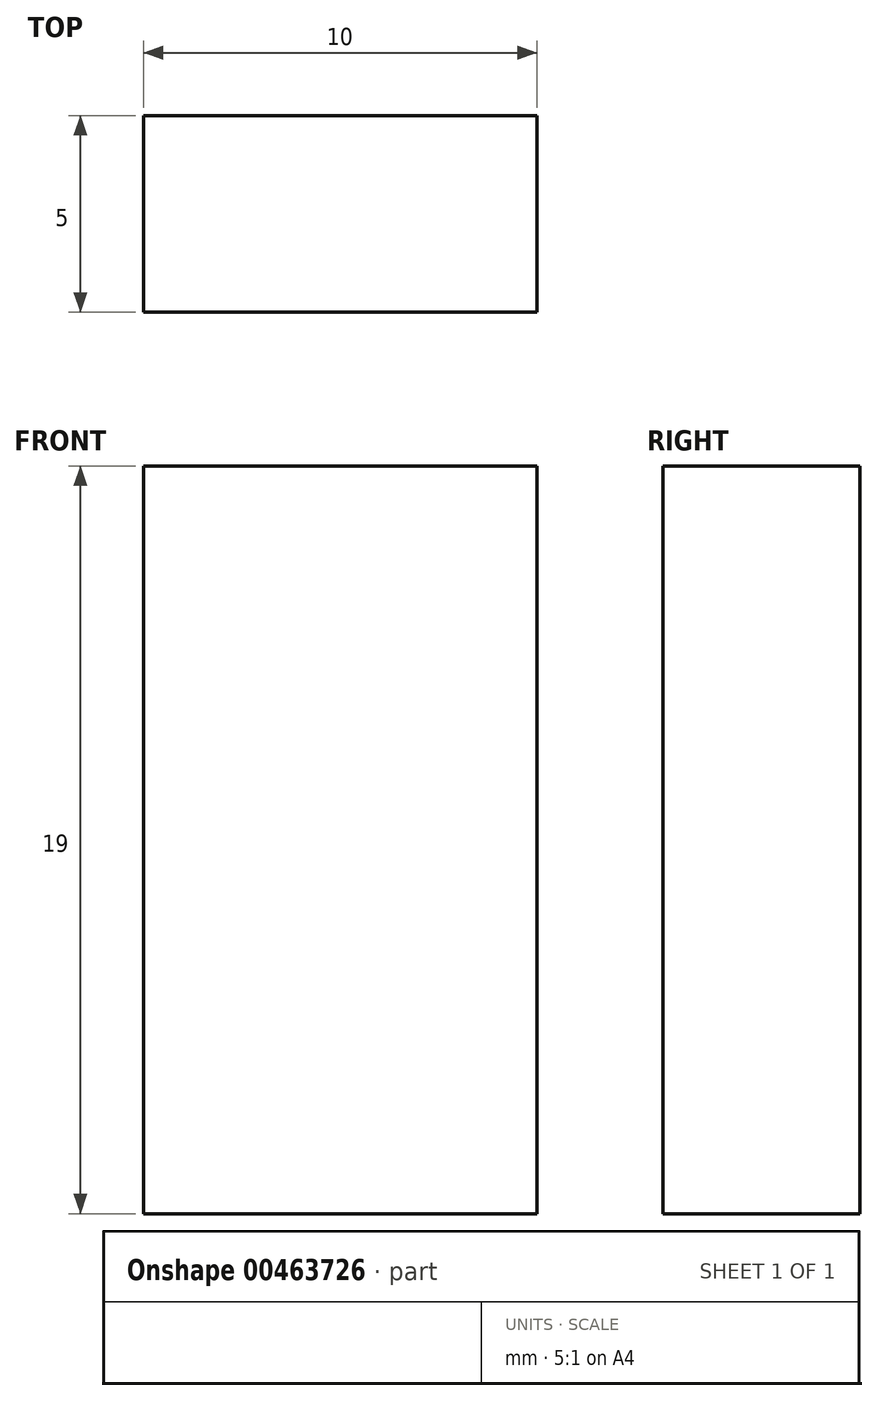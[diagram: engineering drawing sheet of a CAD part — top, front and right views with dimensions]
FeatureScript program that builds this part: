
annotation { "Feature Type Name" : "Feature", "Feature Type Description" : "" }
export const myFeature = defineFeature(function(context is Context, id is Id, definition is map)
    precondition{}
    {
        {
            var Q0;
            Q0=qCreatedBy(makeId("Front.planeOp"),FACE);
            var sketch = newSketch(context, id + "F0", { "sketchPlane" : qUnion([Q0])});
            skLineSegment(sketch, "E0.bottom", {"start": v(5, 9.5) * mm, "end": v(-5, 9.5) * mm});
            skLineSegment(sketch, "E0.top", {"start": v(5, -9.5) * mm, "end": v(-5, -9.5) * mm});
            skLineSegment(sketch, "E0.left", {"start": v(5, 9.5) * mm, "end": v(5, -9.5) * mm});
            skLineSegment(sketch, "E0.right", {"start": v(-5, 9.5) * mm, "end": v(-5, -9.5) * mm});
            skPoint(sketch, "E0.middle", {"position": v(0, 0) * mm});
            skSolve(sketch);
        }
        {
            var Q0;
            Q0=makeQuery(id+"F0.imprint","IMPRINT",FACE,{"disambiguationData":[TD([[makeQuery(id+"F0.imprint","IMPRINT",EDGE,{"derivedFrom":sQuery(id+"F0.wireOp",EDGE,"E0.bottom")}),1.0]])]});
            extrude(context, id + "F1", {"entities" : qUnion([Q0]), "endBound" : BoundingType.SYMMETRIC, "depth" : 5 * mm});
        }
    });
